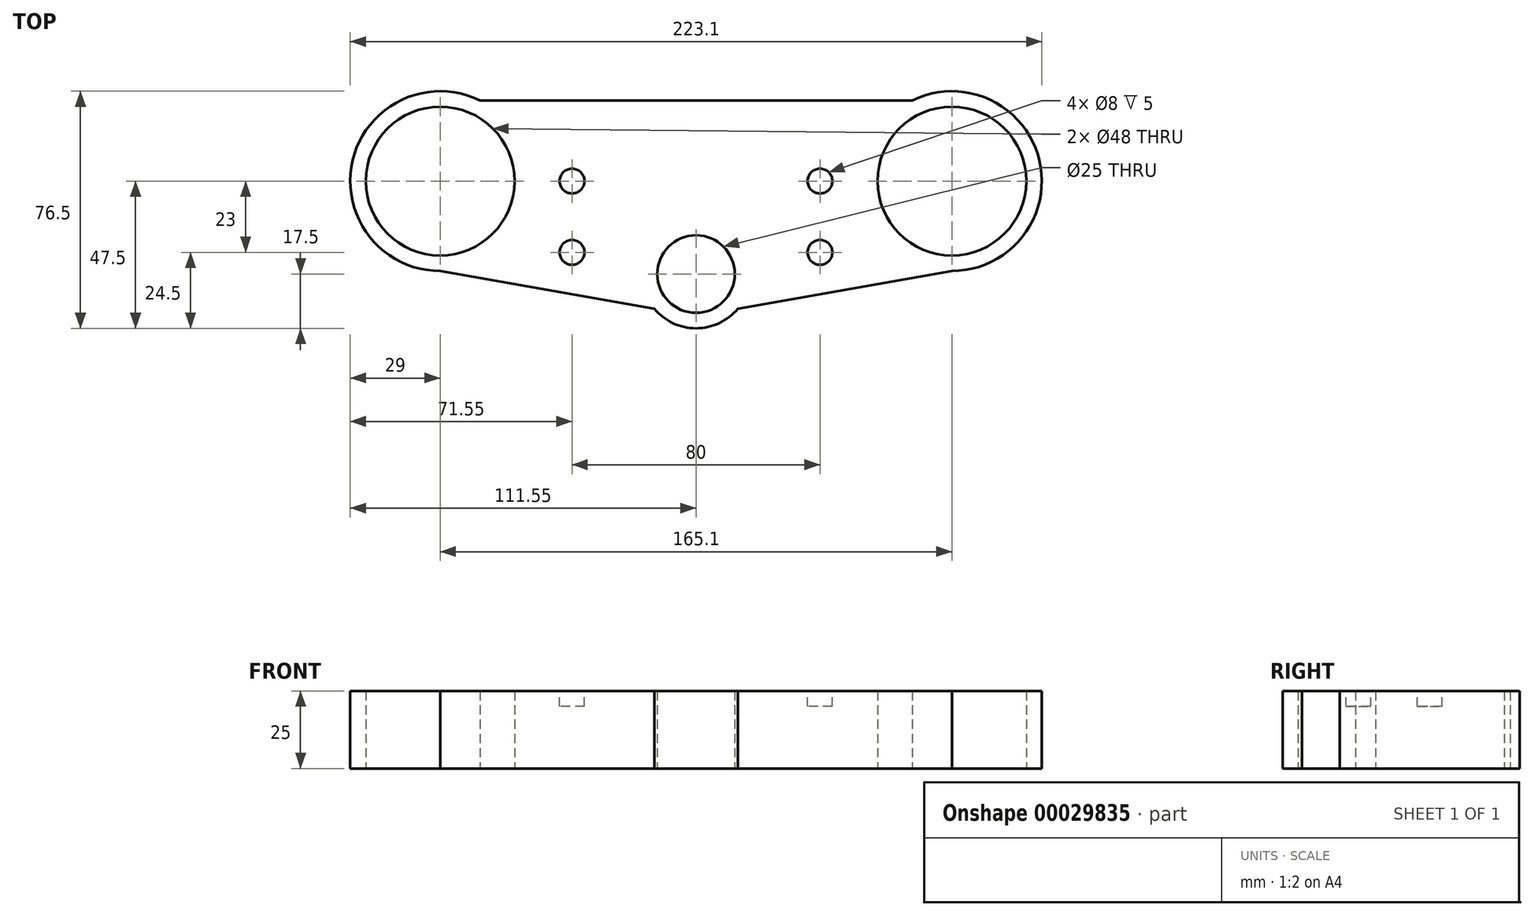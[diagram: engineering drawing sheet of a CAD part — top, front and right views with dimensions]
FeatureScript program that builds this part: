
annotation { "Feature Type Name" : "Feature", "Feature Type Description" : "" }
export const myFeature = defineFeature(function(context is Context, id is Id, definition is map)
    precondition{}
    {
        {
            var Q0;
            Q0=qCreatedBy(makeId("Top.planeOp"),FACE);
            var sketch = newSketch(context, id + "F0", { "sketchPlane" : qUnion([Q0])});
            skCircle(sketch, "E0", {"center": v(-82.55, 0) * mm, "radius": 24 * mm});
            skCircle(sketch, "E1", {"center": v(82.55, 0) * mm, "radius": 24 * mm});
            skLineSegment(sketch, "E2", {"start": v(-82.55, 0) * mm, "end": v(82.55, 0) * mm, "construction": true});
            skArc(sketch, "E3.0", {"start": v(-69.7, 26) * mm, "mid": v(-110.8, 6.6) * mm, "end": v(-82.55, -29) * mm});
            skArc(sketch, "E4.0", {"start": v(82.55, -29) * mm, "mid": v(110.8, 6.6) * mm, "end": v(69.7, 26) * mm});
            skLineSegment(sketch, "E5", {"start": v(-82.55, -29) * mm, "end": v(-13.46, -41.18) * mm});
            skLineSegment(sketch, "E6", {"start": v(-69.7, 26) * mm, "end": v(69.7, 26) * mm});
            skCircle(sketch, "E7", {"center": v(0, -30) * mm, "radius": 12.5 * mm});
            skArc(sketch, "E8.0", {"start": v(-13.46, -41.18) * mm, "mid": v(0, -47.5) * mm, "end": v(13.46, -41.18) * mm});
            skLineSegment(sketch, "E9.trimOffspring", {"start": v(13.46, -41.18) * mm, "end": v(82.55, -29) * mm});
            skSolve(sketch);
        }
        {
            var Q0;
            Q0=qSketchRegion(id+"F0",true);
            extrude(context, id + "F1", {"entities" : qUnion([Q0]), "depth" : 25 * mm});
        }
        {
            var Q0;
            Q0=makeQuery(id+"F1.opExtrude","CAP_FACE",FACE,{"disambiguationData":[OSD([sQuery(id+"F0.wireOp",EDGE,"E0"),sQuery(id+"F0.wireOp",EDGE,"E1"),sQuery(id+"F0.wireOp",EDGE,"E3.0"),sQuery(id+"F0.wireOp",EDGE,"E4.0"),sQuery(id+"F0.wireOp",EDGE,"E5"),sQuery(id+"F0.wireOp",EDGE,"E6"),sQuery(id+"F0.wireOp",EDGE,"E7"),sQuery(id+"F0.wireOp",EDGE,"E8.0"),sQuery(id+"F0.wireOp",EDGE,"E9.trimOffspring")])],"isStart":false});
            var sketch = newSketch(context, id + "F2", { "sketchPlane" : qUnion([Q0])});
            skCircle(sketch, "E10", {"center": v(-40, 0) * mm, "radius": 4 * mm});
            skCircle(sketch, "E11", {"center": v(-40, -23) * mm, "radius": 4 * mm});
            skLineSegment(sketch, "E12", {"start": v(0, 0) * mm, "end": v(0, 26) * mm, "construction": true});
            skCircle(sketch, "E13.0.MirrorC", {"center": v(40, 0) * mm, "radius": 4 * mm});
            skCircle(sketch, "E13.1.MirrorC", {"center": v(40, -23) * mm, "radius": 4 * mm});
            skSolve(sketch);
        }
        {
            var Q0;
            Q0=qSketchRegion(id+"F2",true);
            extrude(context, id + "F3", {"entities" : qUnion([Q0]), "operationType" : NewBodyOperationType.REMOVE, "oppositeDirection" : true, "depth" : 5 * mm});
        }
    });
